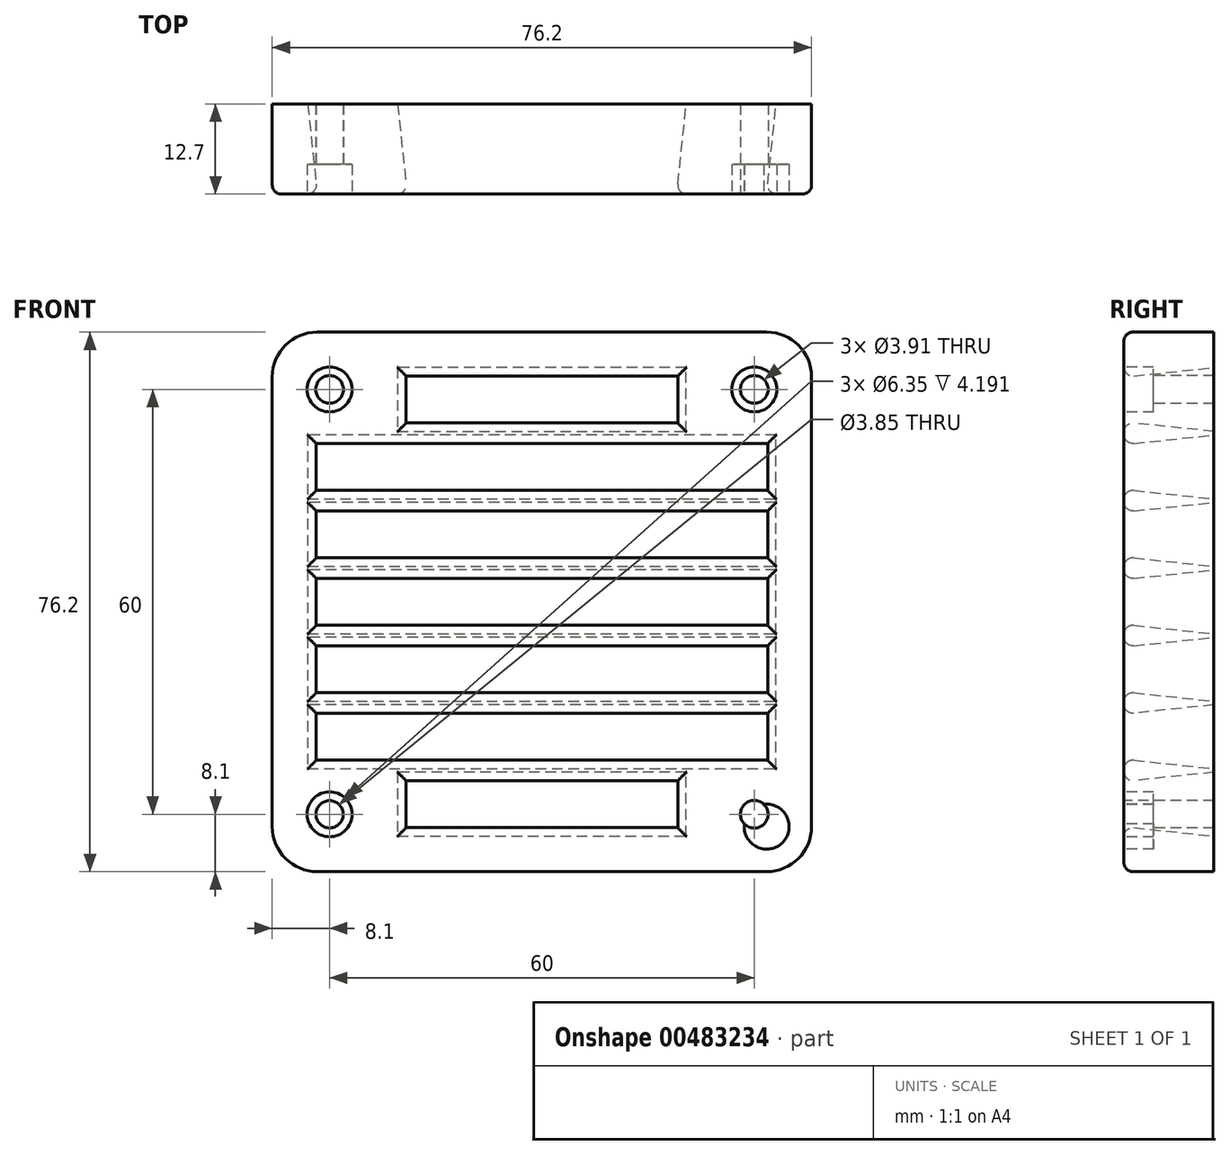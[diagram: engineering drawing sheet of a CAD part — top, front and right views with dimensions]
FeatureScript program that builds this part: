
annotation { "Feature Type Name" : "Feature", "Feature Type Description" : "" }
export const myFeature = defineFeature(function(context is Context, id is Id, definition is map)
    precondition{}
    {
        {
            var Q0;
            Q0=qCreatedBy(makeId("Front.planeOp"),FACE);
            var sketch = newSketch(context, id + "F0", { "sketchPlane" : qUnion([Q0])});
            skLineSegment(sketch, "E0.bottom", {"start": v(31.75, 38.1) * mm, "end": v(-31.75, 38.1) * mm});
            skLineSegment(sketch, "E0.top", {"start": v(31.75, -38.1) * mm, "end": v(-31.75, -38.1) * mm});
            skLineSegment(sketch, "E0.left", {"start": v(38.1, 31.75) * mm, "end": v(38.1, -31.75) * mm});
            skLineSegment(sketch, "E0.right", {"start": v(-38.1, 31.75) * mm, "end": v(-38.1, -31.75) * mm});
            skPoint(sketch, "E0.middle", {"position": v(0, 0) * mm});
            skPoint(sketch, "E1.visualSharp", {"position": v(-38.1, 38.1) * mm});
            skArc(sketch, "E1.filletArc", {"start": v(-31.75, 38.1) * mm, "mid": v(-36.24, 36.24) * mm, "end": v(-38.1, 31.75) * mm});
            skPoint(sketch, "E2.visualSharp", {"position": v(38.1, 38.1) * mm});
            skArc(sketch, "E2.filletArc", {"start": v(38.1, 31.75) * mm, "mid": v(36.24, 36.24) * mm, "end": v(31.75, 38.1) * mm});
            skPoint(sketch, "E3.visualSharp", {"position": v(38.1, -38.1) * mm});
            skArc(sketch, "E3.filletArc", {"start": v(31.75, -38.1) * mm, "mid": v(36.24, -36.24) * mm, "end": v(38.1, -31.75) * mm});
            skPoint(sketch, "E4.visualSharp", {"position": v(-38.1, -38.1) * mm});
            skArc(sketch, "E4.filletArc", {"start": v(-38.1, -31.75) * mm, "mid": v(-36.24, -36.24) * mm, "end": v(-31.75, -38.1) * mm});
            skSolve(sketch);
        }
        {
            var Q0;
            Q0 = qSketchRegion(id + "F0", true);
            extrude(context, id + "F1", {"entities" : qUnion([Q0]), "depth" : 12.7 * mm});
        }
        {
            var Q0;
            Q0=makeQuery(id+"F1.opExtrude","CAP_FACE",FACE,{"disambiguationData":[OSD([sQuery(id+"F0.wireOp",EDGE,"E0.bottom"),sQuery(id+"F0.wireOp",EDGE,"E0.top"),sQuery(id+"F0.wireOp",EDGE,"E0.left"),sQuery(id+"F0.wireOp",EDGE,"E0.right"),sQuery(id+"F0.wireOp",EDGE,"E1.filletArc"),sQuery(id+"F0.wireOp",EDGE,"E2.filletArc"),sQuery(id+"F0.wireOp",EDGE,"E3.filletArc"),sQuery(id+"F0.wireOp",EDGE,"E4.filletArc")])],"isStart":false});
            var sketch = newSketch(context, id + "F2", { "sketchPlane" : qUnion([Q0])});
            skLineSegment(sketch, "E5.bottom", {"start": v(-31.75, -22.22) * mm, "end": v(31.75, -22.22) * mm});
            skLineSegment(sketch, "E5.top", {"start": v(-31.75, -15.87) * mm, "end": v(31.75, -15.87) * mm});
            skLineSegment(sketch, "E5.left", {"start": v(-31.75, -22.22) * mm, "end": v(-31.75, -15.87) * mm});
            skLineSegment(sketch, "E5.right", {"start": v(31.75, -22.22) * mm, "end": v(31.75, -15.87) * mm});
            skLineSegment(sketch, "E6.0.1.0", {"start": v(31.75, -12.7) * mm, "end": v(31.75, -6.35) * mm});
            skLineSegment(sketch, "E6.0.1.1", {"start": v(-31.75, -12.7) * mm, "end": v(-31.75, -6.35) * mm});
            skLineSegment(sketch, "E6.0.1.2", {"start": v(-31.75, -6.35) * mm, "end": v(31.75, -6.35) * mm});
            skLineSegment(sketch, "E6.0.1.3", {"start": v(-31.75, -12.7) * mm, "end": v(31.75, -12.7) * mm});
            skLineSegment(sketch, "E6.0.2.0", {"start": v(31.75, -3.18) * mm, "end": v(31.75, 3.17) * mm});
            skLineSegment(sketch, "E6.0.2.1", {"start": v(-31.75, -3.18) * mm, "end": v(-31.75, 3.17) * mm});
            skLineSegment(sketch, "E6.0.2.2", {"start": v(-31.75, 3.17) * mm, "end": v(31.75, 3.17) * mm});
            skLineSegment(sketch, "E6.0.2.3", {"start": v(-31.75, -3.18) * mm, "end": v(31.75, -3.18) * mm});
            skLineSegment(sketch, "E6.0.3.0", {"start": v(31.75, 6.35) * mm, "end": v(31.75, 12.7) * mm});
            skLineSegment(sketch, "E6.0.3.1", {"start": v(-31.75, 6.35) * mm, "end": v(-31.75, 12.7) * mm});
            skLineSegment(sketch, "E6.0.3.2", {"start": v(-31.75, 12.7) * mm, "end": v(31.75, 12.7) * mm});
            skLineSegment(sketch, "E6.0.3.3", {"start": v(-31.75, 6.35) * mm, "end": v(31.75, 6.35) * mm});
            skLineSegment(sketch, "E6.0.4.0", {"start": v(31.75, 15.87) * mm, "end": v(31.75, 22.22) * mm});
            skLineSegment(sketch, "E6.0.4.1", {"start": v(-31.75, 15.87) * mm, "end": v(-31.75, 22.22) * mm});
            skLineSegment(sketch, "E6.0.4.2", {"start": v(-31.75, 22.22) * mm, "end": v(31.75, 22.22) * mm});
            skLineSegment(sketch, "E6.0.4.3", {"start": v(-31.75, 15.87) * mm, "end": v(31.75, 15.87) * mm});
            skLineSegment(sketch, "E6.direction1", {"start": v(-31.75, -22.22) * mm, "end": v(-6.35, -22.22) * mm, "construction": true});
            skLineSegment(sketch, "E6.direction2", {"start": v(-31.75, -22.22) * mm, "end": v(-31.75, -12.7) * mm, "construction": true});
            skLineSegment(sketch, "E7.bottom", {"start": v(-19.05, 31.75) * mm, "end": v(19.05, 31.75) * mm});
            skLineSegment(sketch, "E7.top", {"start": v(-19.05, 25.4) * mm, "end": v(19.05, 25.4) * mm});
            skLineSegment(sketch, "E7.left", {"start": v(-19.05, 31.75) * mm, "end": v(-19.05, 25.4) * mm});
            skLineSegment(sketch, "E7.right", {"start": v(19.05, 31.75) * mm, "end": v(19.05, 25.4) * mm});
            skLineSegment(sketch, "E8.bottom", {"start": v(-19.05, -25.4) * mm, "end": v(19.05, -25.4) * mm});
            skLineSegment(sketch, "E8.top", {"start": v(-19.05, -31.75) * mm, "end": v(19.05, -31.75) * mm});
            skLineSegment(sketch, "E8.left", {"start": v(-19.05, -25.4) * mm, "end": v(-19.05, -31.75) * mm});
            skLineSegment(sketch, "E8.right", {"start": v(19.05, -25.4) * mm, "end": v(19.05, -31.75) * mm});
            skSolve(sketch);
        }
        {
            var Q0;
            Q0 = qSketchRegion(id + "F2", true);
            extrude(context, id + "F3", {"entities" : qUnion([Q0]), "operationType" : NewBodyOperationType.REMOVE, "endBound" : BoundingType.THROUGH_ALL, "oppositeDirection" : true, "depth" : 6.35 * mm, "hasDraft" : true, "draftAngle" : 6 * degree});
        }
        {
            var Q0;
            Q0=makeQuery(id+"F1.opExtrude","CAP_FACE",FACE,{"disambiguationData":[OSD([sQuery(id+"F0.wireOp",EDGE,"E0.bottom"),sQuery(id+"F0.wireOp",EDGE,"E0.top"),sQuery(id+"F0.wireOp",EDGE,"E0.left"),sQuery(id+"F0.wireOp",EDGE,"E0.right"),sQuery(id+"F0.wireOp",EDGE,"E1.filletArc"),sQuery(id+"F0.wireOp",EDGE,"E2.filletArc"),sQuery(id+"F0.wireOp",EDGE,"E3.filletArc"),sQuery(id+"F0.wireOp",EDGE,"E4.filletArc")])],"isStart":false});
            fillet(context, id + "F4", {"entities" : qUnion([Q0]), "radius" : 1.27 * mm, "tangentPropagation" : true, "allowEdgeOverflow" : false});
        }
        {
            var Q0;
            Q0=makeQuery(id+"F1.opExtrude","CAP_FACE",FACE,{"disambiguationData":[OSD([sQuery(id+"F0.wireOp",EDGE,"E0.bottom"),sQuery(id+"F0.wireOp",EDGE,"E0.top"),sQuery(id+"F0.wireOp",EDGE,"E0.left"),sQuery(id+"F0.wireOp",EDGE,"E0.right"),sQuery(id+"F0.wireOp",EDGE,"E1.filletArc"),sQuery(id+"F0.wireOp",EDGE,"E2.filletArc"),sQuery(id+"F0.wireOp",EDGE,"E3.filletArc"),sQuery(id+"F0.wireOp",EDGE,"E4.filletArc")])],"isStart":false});
            var sketch = newSketch(context, id + "F5", { "sketchPlane" : qUnion([Q0])});
            skCircle(sketch, "E9", {"center": v(-30, 30) * mm, "radius": 1.96 * mm});
            skCircle(sketch, "E10", {"center": v(30, 30) * mm, "radius": 1.96 * mm});
            skCircle(sketch, "E11", {"center": v(-30, -30) * mm, "radius": 1.93 * mm});
            skCircle(sketch, "E12", {"center": v(30, -30) * mm, "radius": 1.96 * mm});
            skSolve(sketch);
        }
        {
            var Q0;
            Q0 = qSketchRegion(id + "F5", true);
            extrude(context, id + "F6", {"entities" : qUnion([Q0]), "operationType" : NewBodyOperationType.REMOVE, "endBound" : BoundingType.THROUGH_ALL, "oppositeDirection" : true, "depth" : 25.4 * mm});
        }
        {
            var Q0;
            Q0=makeQuery(id+"F1.opExtrude","CAP_FACE",FACE,{"disambiguationData":[OSD([sQuery(id+"F0.wireOp",EDGE,"E0.bottom"),sQuery(id+"F0.wireOp",EDGE,"E0.top"),sQuery(id+"F0.wireOp",EDGE,"E0.left"),sQuery(id+"F0.wireOp",EDGE,"E0.right"),sQuery(id+"F0.wireOp",EDGE,"E1.filletArc"),sQuery(id+"F0.wireOp",EDGE,"E2.filletArc"),sQuery(id+"F0.wireOp",EDGE,"E3.filletArc"),sQuery(id+"F0.wireOp",EDGE,"E4.filletArc")])],"isStart":false});
            var sketch = newSketch(context, id + "F7", { "sketchPlane" : qUnion([Q0])});
            skCircle(sketch, "E13", {"center": v(-30, 30) * mm, "radius": 3.18 * mm});
            skCircle(sketch, "E14", {"center": v(30, 30) * mm, "radius": 3.18 * mm});
            skCircle(sketch, "E15", {"center": v(31.75, -31.75) * mm, "radius": 3.18 * mm});
            skCircle(sketch, "E16", {"center": v(-30, -30) * mm, "radius": 3.18 * mm});
            skSolve(sketch);
        }
        {
            var Q0;
            Q0 = qSketchRegion(id + "F7", true);
            extrude(context, id + "F8", {"entities" : qUnion([Q0]), "operationType" : NewBodyOperationType.REMOVE, "oppositeDirection" : true, "depth" : 4.2 * mm});
        }
    });
